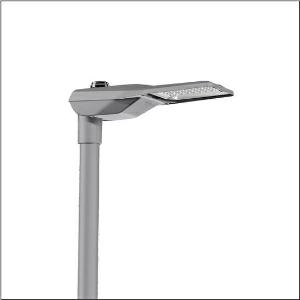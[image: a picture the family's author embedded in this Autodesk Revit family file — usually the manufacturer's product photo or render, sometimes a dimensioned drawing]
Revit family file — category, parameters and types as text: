
# Revit family: streetlight_sl_21_mini___st1_5a_5xe6p37n08hb_7a86
name_source: partatom
category: Lighting Fixtures
units: mm (PartAtom-declared; Revit-internal decimal feet)

## family parameters
Cut with Voids When Loaded = No
Host = Face
Light Source = No
Part Type = Normal
Room Calculation Point = No
Round Connector Dimension = Use Diameter
Shared = No

## types (1)
- --- (1 x LED, 8890 lm, 66 W, 3000K)
    Apparent Load = 66 VA
    CIE Flux Codes = 22 53 95 100 100
    Color Rendering = 70
    Color Temperature = 3000K
    Default Elevation = 1800 mm
    Description = Streetlight SL 21 mini, mast luminaire, primary light control with lens, of PMMA, primary optical cover: cover, of toughened safety glass, transparent, light distribution: ST1.5a, light emission: direct distribution, primary light characteristic: asymmetric, installation type: side-entry, LED, 3G 1.5mm², High Power LED, rated luminous flux: 8.890lm, luminous efficacy: 135lm/W, light colour: 730, colour temperature: 3000K, control gear: NEMA (7pin), control: overheat protection, pre-setting: linear dimming characteristic, constant luminous flux control, time-dependent luminous flux control, flexible luminous flux parameterisation, mains connection: 230..240V, AC, 50/60Hz, connection cable pre-assembled, cable length: 8,5m, wiring characteristics: H07RN-F, start of lifetime: 66W, end of service life: 69W, reduction: 30W, luminaire housing, of diecast aluminium (EN AC-44300), powder-coated, Siteco® metallic grey (DB 702S), corrosivity category C5 mid according to DIN EN ISO 12944, multi-level sealing system, sealing non-destructively replaceable, inclination adjustable: 0°, 5°, 10°, 15°, length: 628mm, width: 235mm, height: 110mm, spigot size: 42mm (side-entry), mounting height: 4..8m, protection rating (complete): IP66, insulation class (complete): insulation class I (protective earthing), certification: CE, ENEC, ENEC+, VDE, impact resistance: IK09, permissible operating ambient temperature for outdoor applications: -40..+50°C, standard-compliant lighting for roads and squares, packaging unit: 1 piece

Light Distribution: ST1.5a
    Height = 110 mm
    Lamp = 1 x LED
    Lamp Light Flux = 8890 lm
    Lamp Power = 66 W
    Lamp count = 1
    Length = 625 mm
    Luminous efficacy = 135 lm/W
    Manufacturer = Siteco
    ModVariant = No
    Model = 5XE6P37N08HB
    Number of Poles = 1
    OnlyDefault = Yes
    Power Factor = 1
    Product Name = Streetlight SL 21 mini | ST1.5a
    Product group = mast luminaire | pylon top
    ProductGroupID = 6100
    Protection Class = Protection class I
    Protection Degree = IP 66
    RLX_Detail_Level = 1
    RLX_Emergency_Light_Flux = 0 lm
    RLX_Emergency_Type = 0
    RLX_Emergency_Type_DB = No
    RlxData = <blob elided: 95573 chars, md5=ddee2eea>
    Socket = socket
    Standby Power = 0 W
    System Light Flux = 8890 lm
    System Power = 66 W
    Type Comments = factory setting: luminous flux: 100 % | dim-lin: 254 | 670 mA
    Type Image = l_1294379.jpg
    URL = http://relux.com
    VarID = @adj_128924
    Voltage = 0 V
    Weight = 0.00 kg
    Width = 234 mm

## geometry (parser evidence)
native form markers: Blend x4, Sweep x9
no freeform markers — native parametric forms only
